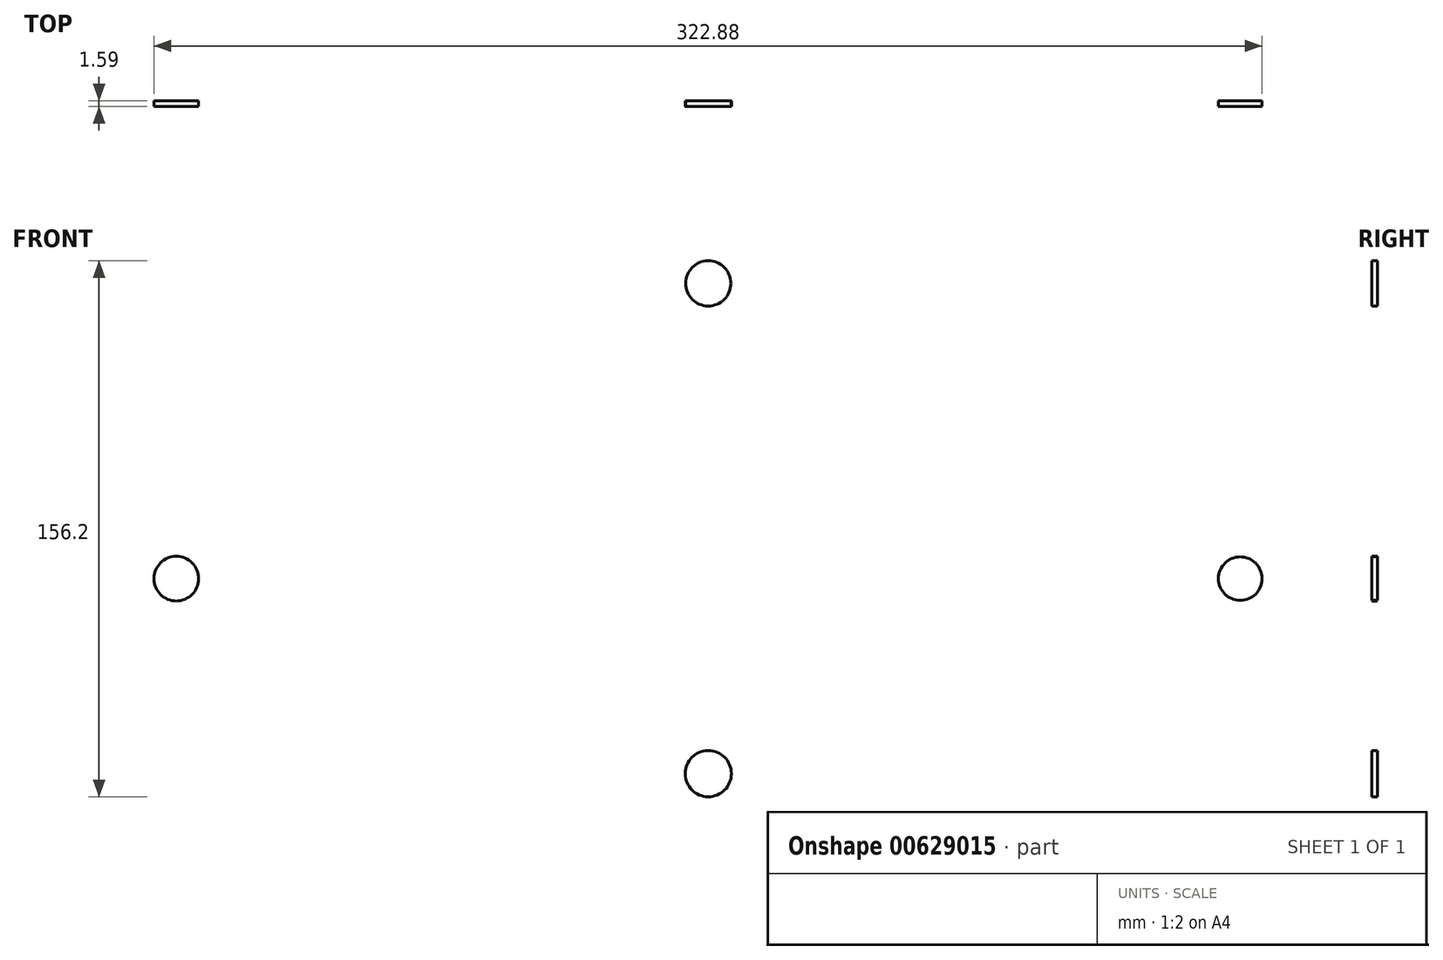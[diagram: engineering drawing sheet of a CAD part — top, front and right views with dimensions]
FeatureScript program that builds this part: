
annotation { "Feature Type Name" : "Feature", "Feature Type Description" : "" }
export const myFeature = defineFeature(function(context is Context, id is Id, definition is map)
    precondition{}
    {
        {
            var Q0;
            Q0=qCreatedBy(makeId("Front.planeOp"),FACE);
            var sketch = newSketch(context, id + "F0", { "sketchPlane" : qUnion([Q0])});
            skCircle(sketch, "E0", {"center": v(0, 71.44) * mm, "radius": 6.59 * mm});
            skCircle(sketch, "E1", {"center": v(155.01, -14.6) * mm, "radius": 6.35 * mm});
            skCircle(sketch, "E2", {"center": v(0, -71.44) * mm, "radius": 6.73 * mm});
            skCircle(sketch, "E3", {"center": v(-155.01, -14.6) * mm, "radius": 6.5 * mm});
            skSolve(sketch);
        }
        {
            var Q0;
            Q0=makeQuery(id+"F0.imprint","IMPRINT",FACE,{"disambiguationData":[TD([[makeQuery(id+"F0.imprint","IMPRINT",EDGE,{"derivedFrom":sQuery(id+"F0.wireOp",EDGE,"E3")}),1.0]])]});
            var Q1;
            Q1=makeQuery(id+"F0.imprint","IMPRINT",FACE,{"disambiguationData":[TD([[makeQuery(id+"F0.imprint","IMPRINT",EDGE,{"derivedFrom":sQuery(id+"F0.wireOp",EDGE,"E0")}),1.0]])]});
            var Q2;
            Q2=makeQuery(id+"F0.imprint","IMPRINT",FACE,{"disambiguationData":[TD([[makeQuery(id+"F0.imprint","IMPRINT",EDGE,{"derivedFrom":sQuery(id+"F0.wireOp",EDGE,"E1")}),1.0]])]});
            var Q3;
            Q3=makeQuery(id+"F0.imprint","IMPRINT",FACE,{"disambiguationData":[TD([[makeQuery(id+"F0.imprint","IMPRINT",EDGE,{"derivedFrom":sQuery(id+"F0.wireOp",EDGE,"E2")}),1.0]])]});
            extrude(context, id + "F1", {"entities" : qUnion([Q0, Q1, Q2, Q3]), "depth" : 1.59 * mm, "offsetDistance" : 25.4 * mm});
        }
    });
